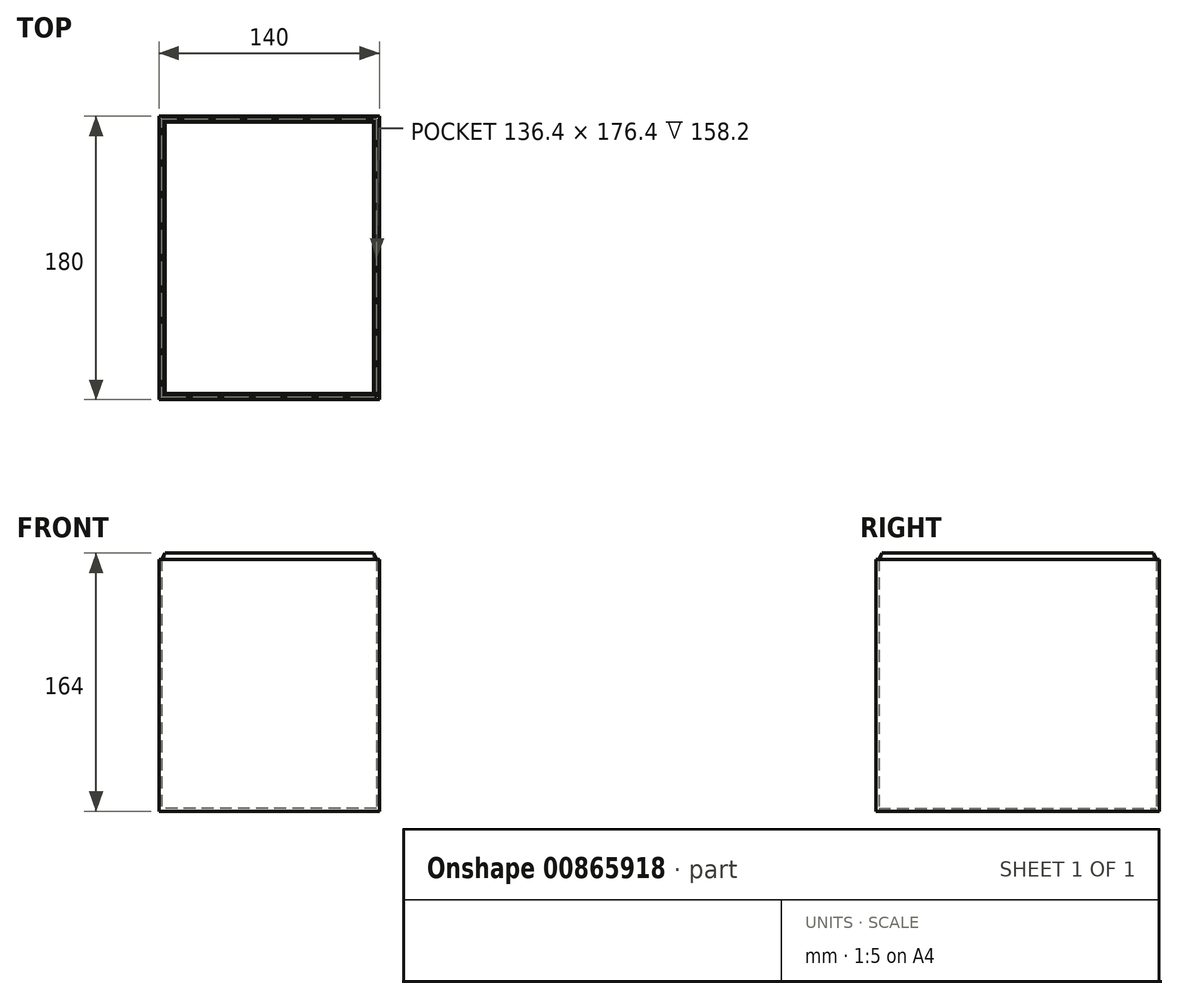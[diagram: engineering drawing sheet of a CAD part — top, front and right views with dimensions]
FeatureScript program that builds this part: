
annotation { "Feature Type Name" : "Feature", "Feature Type Description" : "" }
export const myFeature = defineFeature(function(context is Context, id is Id, definition is map)
    precondition{}
    {
        {
            var Q0;
            Q0=qCreatedBy(makeId("Top.planeOp"),FACE);
            var sketch = newSketch(context, id + "F0", { "sketchPlane" : qUnion([Q0])});
            skLineSegment(sketch, "E0.bottom", {"start": v(70, -90) * mm, "end": v(-70, -90) * mm});
            skLineSegment(sketch, "E0.top", {"start": v(70, 90) * mm, "end": v(-70, 90) * mm});
            skLineSegment(sketch, "E0.left", {"start": v(70, -90) * mm, "end": v(70, 90) * mm});
            skLineSegment(sketch, "E0.right", {"start": v(-70, -90) * mm, "end": v(-70, 90) * mm});
            skPoint(sketch, "E0.middle", {"position": v(0, 0) * mm});
            skSolve(sketch);
        }
        {
            var Q0;
            Q0=makeQuery(id+"F0.imprint","IMPRINT",FACE,{"disambiguationData":[TD([[makeQuery(id+"F0.imprint","IMPRINT",EDGE,{"derivedFrom":sQuery(id+"F0.wireOp",EDGE,"E0.bottom")}),-1.0]])]});
            extrude(context, id + "F1", {"entities" : qUnion([Q0]), "depth" : 160 * mm, "offsetDistance" : 25 * mm});
        }
        {
            var Q0;
            Q0=makeQuery(id+"F1.opExtrude","CAP_FACE",FACE,{"disambiguationData":[OSD([sQuery(id+"F0.wireOp",EDGE,"E0.bottom"),sQuery(id+"F0.wireOp",EDGE,"E0.top"),sQuery(id+"F0.wireOp",EDGE,"E0.left"),sQuery(id+"F0.wireOp",EDGE,"E0.right")])],"isStart":false});
            shell(context, id + "F2", {"entities" : qUnion([Q0]), "thickness" : 1.8 * mm});
        }
        {
            var Q0;
            Q0=makeQuery(id+"F1.opExtrude","CAP_FACE",FACE,{"disambiguationData":[OSD([sQuery(id+"F0.wireOp",EDGE,"E0.bottom"),sQuery(id+"F0.wireOp",EDGE,"E0.top"),sQuery(id+"F0.wireOp",EDGE,"E0.left"),sQuery(id+"F0.wireOp",EDGE,"E0.right")])],"isStart":false});
            var sketch = newSketch(context, id + "F3", { "sketchPlane" : qUnion([Q0])});
            skLineSegment(sketch, "E1.0", {"start": v(-70, -90) * mm, "end": v(-70, 90) * mm});
            skLineSegment(sketch, "E2.0", {"start": v(-68.2, -88.2) * mm, "end": v(-68.2, 88.2) * mm});
            skLineSegment(sketch, "E3.0", {"start": v(70, -90) * mm, "end": v(-70, -90) * mm});
            skLineSegment(sketch, "E4.0", {"start": v(68.2, -88.2) * mm, "end": v(-68.2, -88.2) * mm});
            skLineSegment(sketch, "E5.0", {"start": v(70, 90) * mm, "end": v(-70, 90) * mm});
            skLineSegment(sketch, "E6.0", {"start": v(68.2, 88.2) * mm, "end": v(-68.2, 88.2) * mm});
            skLineSegment(sketch, "E7.0", {"start": v(70, -90) * mm, "end": v(70, 90) * mm});
            skLineSegment(sketch, "E8.0", {"start": v(68.2, -88.2) * mm, "end": v(68.2, 88.2) * mm});
            skSolve(sketch);
        }
        {
            var Q0;
            Q0=makeQuery(id+"F3.imprint","IMPRINT",FACE,{"disambiguationData":[TD([[makeQuery(id+"F3.imprint","IMPRINT",EDGE,{"derivedFrom":sQuery(id+"F3.wireOp",EDGE,"E1.0")}),-1.0]])]});
            cPlane(context, id + "F4", {"entities" : qUnion([Q0]), "cplaneType" : CPlaneType.OFFSET, "offset" : 4 * mm, "width" : 150 * mm, "height" : 150 * mm});
        }
        {
            var Q0;
            Q0=qCreatedBy(id+"F4.planeOp",FACE);
            var sketch = newSketch(context, id + "F5", { "sketchPlane" : qUnion([Q0])});
            skLineSegment(sketch, "E9.0", {"start": v(70, 90) * mm, "end": v(-70, 90) * mm});
            skLineSegment(sketch, "E10.0", {"start": v(70, -90) * mm, "end": v(70, 90) * mm});
            skLineSegment(sketch, "E11.0", {"start": v(70, -90) * mm, "end": v(-70, -90) * mm});
            skLineSegment(sketch, "E12.0", {"start": v(-70, -90) * mm, "end": v(-70, 90) * mm});
            skLineSegment(sketch, "E13.0", {"start": v(-66.2, -86.2) * mm, "end": v(-66.2, 86.2) * mm});
            skLineSegment(sketch, "E13.1", {"start": v(66.2, -86.2) * mm, "end": v(-66.2, -86.2) * mm});
            skLineSegment(sketch, "E13.2", {"start": v(66.2, -86.2) * mm, "end": v(66.2, 86.2) * mm});
            skLineSegment(sketch, "E13.3", {"start": v(66.2, 86.2) * mm, "end": v(-66.2, 86.2) * mm});
            skSolve(sketch);
        }
        {
            var Q0;
            Q0=sQuery(id+"F3.wireOp",EDGE,"E1.0");
            var Q1;
            Q1=sQuery(id+"F3.wireOp",EDGE,"E3.0");
            var Q2;
            Q2=sQuery(id+"F3.wireOp",EDGE,"E7.0");
            var Q3;
            Q3=sQuery(id+"F3.wireOp",EDGE,"E5.0");
            extrude(context, id + "F6", {"bodyType" : ToolBodyType.SURFACE, "surfaceEntities" : qUnion([Q0, Q1, Q2, Q3]), "depth" : 4 * mm, "offsetDistance" : 25 * mm});
        }
        {
            var Q0;
            Q0=makeQuery(id+"F3.imprint","IMPRINT",FACE,{"disambiguationData":[TD([[makeQuery(id+"F3.imprint","IMPRINT",EDGE,{"derivedFrom":sQuery(id+"F3.wireOp",EDGE,"E2.0")}),-1.0]])]});
            var Q1;
            Q1=makeQuery(id+"F5.imprint","IMPRINT",FACE,{"disambiguationData":[TD([[makeQuery(id+"F5.imprint","IMPRINT",EDGE,{"derivedFrom":sQuery(id+"F5.wireOp",EDGE,"E13.0")}),-1.0]])]});
            loft(context, id + "F7", {"sheetProfilesArray" : [{ "sheetProfileEntities" : qUnion([Q0]) }, { "sheetProfileEntities" : qUnion([Q1]) }]});
        }
        {
            var Q0;
            Q0=makeQuery(id+"F5.imprint","IMPRINT",FACE,{"disambiguationData":[TD([[makeQuery(id+"F5.imprint","IMPRINT",EDGE,{"derivedFrom":sQuery(id+"F5.wireOp",EDGE,"E13.0")}),-1.0]])]});
            extrude(context, id + "F8", {"entities" : qUnion([Q0]), "operationType" : NewBodyOperationType.REMOVE, "oppositeDirection" : true, "depth" : 25 * mm, "offsetDistance" : 25 * mm});
        }
    });
